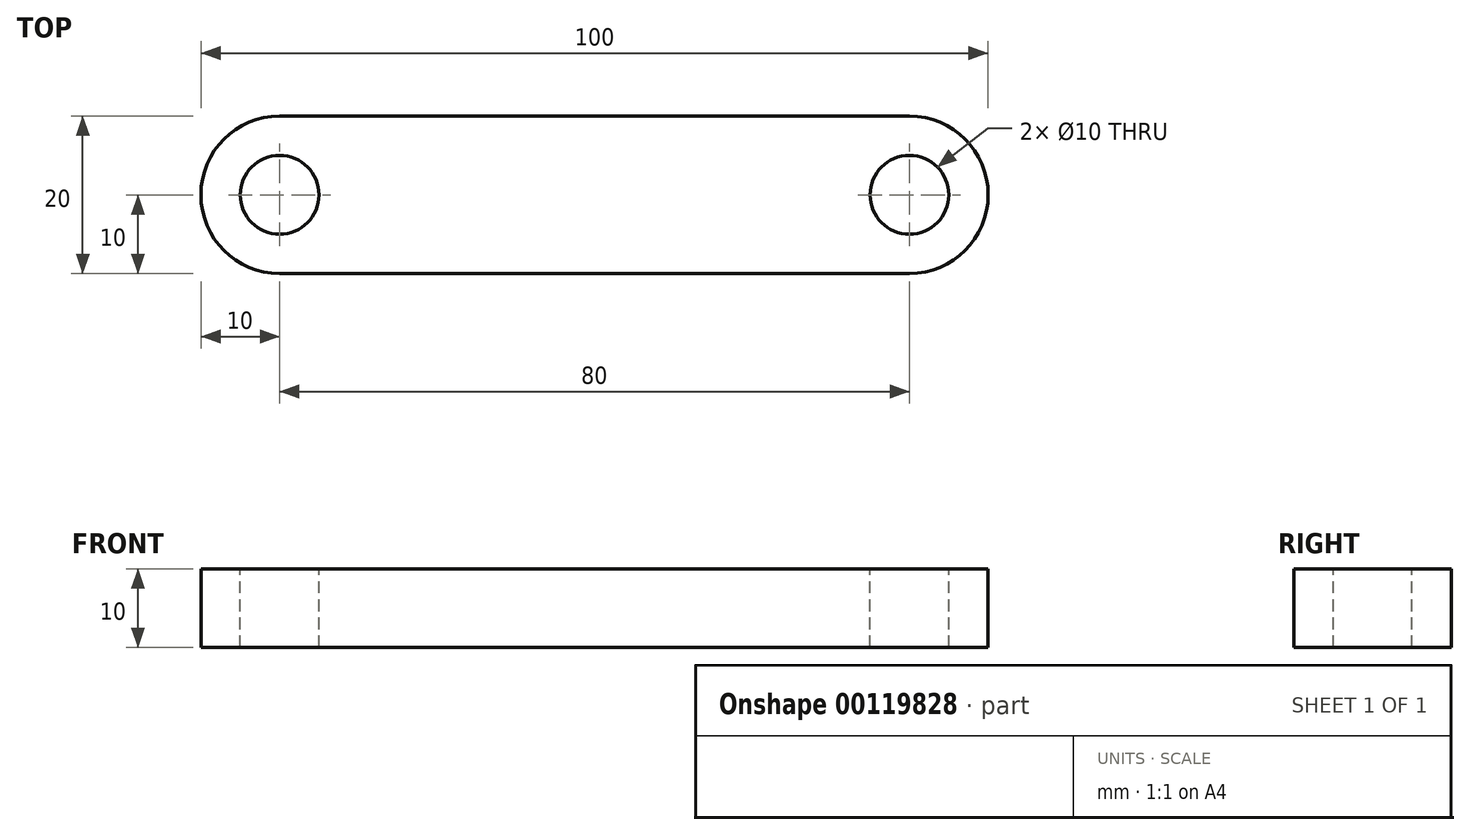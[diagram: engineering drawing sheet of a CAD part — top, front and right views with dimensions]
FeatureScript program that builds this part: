
annotation { "Feature Type Name" : "Feature", "Feature Type Description" : "" }
export const myFeature = defineFeature(function(context is Context, id is Id, definition is map)
    precondition{}
    {
        {
            var Q0;
            Q0=qCreatedBy(makeId("Top.planeOp"),FACE);
            var sketch = newSketch(context, id + "F0", { "sketchPlane" : qUnion([Q0])});
            skArc(sketch, "E0", {"start": v(0, 10) * mm, "mid": v(-10, 0) * mm, "end": v(0, -10) * mm});
            skLineSegment(sketch, "E1", {"start": v(0, 10) * mm, "end": v(80, 10) * mm});
            skLineSegment(sketch, "E2", {"start": v(0, -10) * mm, "end": v(80, -10) * mm});
            skArc(sketch, "E3", {"start": v(80, -10) * mm, "mid": v(90, 0) * mm, "end": v(80, 10) * mm});
            skSolve(sketch);
        }
        {
            var Q0;
            Q0=makeQuery(id+"F0.imprint","IMPRINT",FACE,{"disambiguationData":[TD([[makeQuery(id+"F0.imprint","IMPRINT",EDGE,{"derivedFrom":sQuery(id+"F0.wireOp",EDGE,"E0")}),1.0]])]});
            extrude(context, id + "F1", {"entities" : qUnion([Q0]), "oppositeDirection" : true, "depth" : 10 * mm});
        }
        {
            var Q0;
            Q0=makeQuery(id+"F1.opExtrude","CAP_FACE",FACE,{"disambiguationData":[OSD([sQuery(id+"F0.wireOp",EDGE,"E0"),sQuery(id+"F0.wireOp",EDGE,"E1"),sQuery(id+"F0.wireOp",EDGE,"E2"),sQuery(id+"F0.wireOp",EDGE,"E3")])],"isStart":true});
            var sketch = newSketch(context, id + "F2", { "sketchPlane" : qUnion([Q0])});
            skCircle(sketch, "E4", {"center": v(0, 0) * mm, "radius": 5 * mm});
            skCircle(sketch, "E5", {"center": v(80, 0) * mm, "radius": 5 * mm});
            skSolve(sketch);
        }
        {
            var Q0;
            Q0 = qSketchRegion(id + "F2", true);
            extrude(context, id + "F3", {"entities" : qUnion([Q0]), "operationType" : NewBodyOperationType.REMOVE, "endBound" : BoundingType.THROUGH_ALL, "oppositeDirection" : true, "depth" : 25 * mm});
        }
    });
